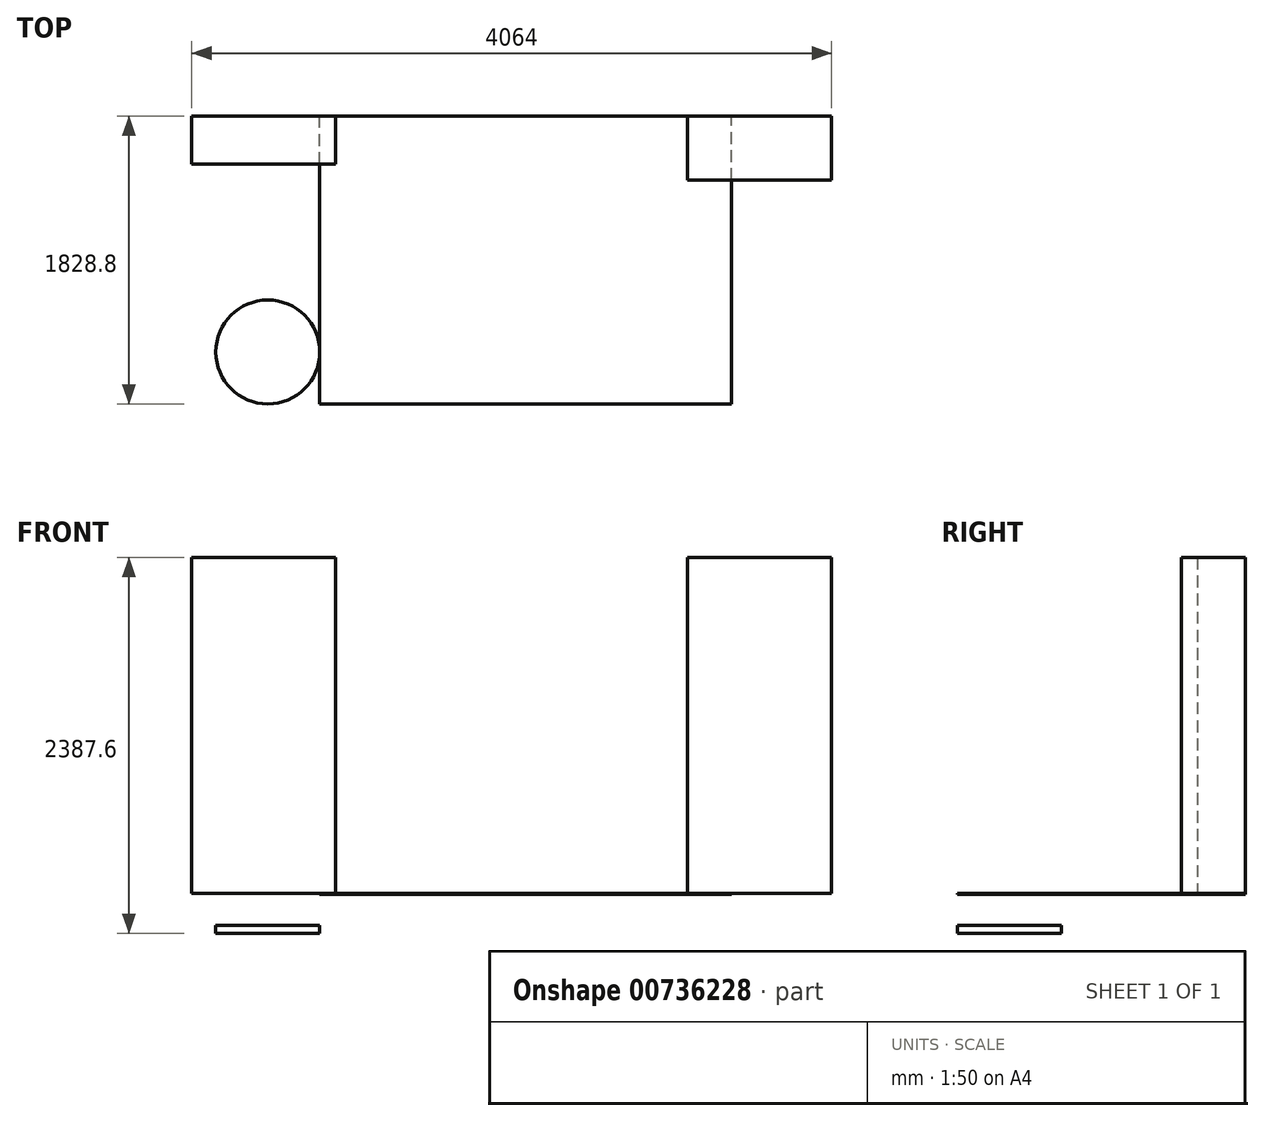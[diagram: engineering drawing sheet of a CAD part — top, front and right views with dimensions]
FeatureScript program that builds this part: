
annotation { "Feature Type Name" : "Feature", "Feature Type Description" : "" }
export const myFeature = defineFeature(function(context is Context, id is Id, definition is map)
    precondition{}
    {
        {
            assignVariable(context, id + "F0", {"name" : "StoopT", "anyValue" : 6});
        }
        {
            var Q0;
            Q0=qCreatedBy(makeId("Top.planeOp"),FACE);
            var sketch = newSketch(context, id + "F1", { "sketchPlane" : qUnion([Q0])});
            skLineSegment(sketch, "E0.bottom", {"start": v(1308.1, -914.4) * mm, "end": v(-1308.1, -914.4) * mm});
            skLineSegment(sketch, "E0.top", {"start": v(1308.1, 914.4) * mm, "end": v(-1308.1, 914.4) * mm});
            skLineSegment(sketch, "E0.left", {"start": v(1308.1, -914.4) * mm, "end": v(1308.1, 914.4) * mm});
            skLineSegment(sketch, "E0.right", {"start": v(-1308.1, -914.4) * mm, "end": v(-1308.1, 914.4) * mm});
            skPoint(sketch, "E0.middle", {"position": v(0, 0) * mm});
            skSolve(sketch);
        }
        {
            var Q0;
            Q0=makeQuery(id+"F1.imprint","IMPRINT",FACE,{"disambiguationData":[TD([[makeQuery(id+"F1.imprint","IMPRINT",EDGE,{"derivedFrom":sQuery(id+"F1.wireOp",EDGE,"E0.bottom")}),-1.0]])]});
            extrude(context, id + "F2", {"entities" : qUnion([Q0]), "depth" : (getVariable(context, 'StoopT')) * mm, "offsetDistance" : 25.4 * mm});
        }
        {
            var Q0;
            Q0=makeQuery(id+"F2.opExtrude","CAP_FACE",FACE,{"disambiguationData":[OSD([sQuery(id+"F1.wireOp",EDGE,"E0.bottom"),sQuery(id+"F1.wireOp",EDGE,"E0.top"),sQuery(id+"F1.wireOp",EDGE,"E0.left"),sQuery(id+"F1.wireOp",EDGE,"E0.right")])],"isStart":false});
            var sketch = newSketch(context, id + "F3", { "sketchPlane" : qUnion([Q0])});
            skLineSegment(sketch, "E1.top", {"start": v(-2120.9, 609.6) * mm, "end": v(-1206.5, 609.6) * mm});
            skLineSegment(sketch, "E1.left", {"start": v(-2120.9, 914.4) * mm, "end": v(-2120.9, 609.6) * mm});
            skLineSegment(sketch, "E1.right", {"start": v(-1206.5, 914.4) * mm, "end": v(-1206.5, 609.6) * mm});
            skLineSegment(sketch, "E2.bottom", {"start": v(1943.1, 914.4) * mm, "end": v(1028.7, 914.4) * mm});
            skLineSegment(sketch, "E2.top", {"start": v(1943.1, 508) * mm, "end": v(1028.7, 508) * mm});
            skLineSegment(sketch, "E2.left", {"start": v(1943.1, 914.4) * mm, "end": v(1943.1, 508) * mm});
            skLineSegment(sketch, "E2.right", {"start": v(1028.7, 914.4) * mm, "end": v(1028.7, 508) * mm});
            skLineSegment(sketch, "E3", {"start": v(-2120.9, 914.4) * mm, "end": v(-1206.5, 914.4) * mm});
            skSolve(sketch);
        }
        {
            var Q0;
            {var subQ0=sQuery(id+"F3.wireOp",EDGE,"E1.left");Q0=makeQuery(id+"F3.imprint","IMPRINT",FACE,{"disambiguationData":[TD([[makeQuery(id+"F3.imprint","IMPRINT",EDGE,{"derivedFrom":subQ0}),1.0]])]});}
            var Q1;
            {var subQ0=sQuery(id+"F3.wireOp",EDGE,"E1.right");Q1=makeQuery(id+"F3.imprint","IMPRINT",FACE,{"disambiguationData":[TD([[makeQuery(id+"F3.imprint","IMPRINT",EDGE,{"derivedFrom":subQ0}),-1.0]])]});}
            var Q2;
            {var subQ3=sQuery(id+"F3.wireOp",EDGE,"E2.right");Q2=makeQuery(id+"F3.imprint","IMPRINT",FACE,{"disambiguationData":[TD([[makeQuery(id+"F3.imprint","IMPRINT",EDGE,{"derivedFrom":subQ3}),1.0]])]});}
            var Q3;
            {var subQ3=sQuery(id+"F3.wireOp",EDGE,"E2.left");Q3=makeQuery(id+"F3.imprint","IMPRINT",FACE,{"disambiguationData":[TD([[makeQuery(id+"F3.imprint","IMPRINT",EDGE,{"derivedFrom":subQ3}),-1.0]])]});}
            extrude(context, id + "F4", {"entities" : qUnion([Q0, Q1, Q2, Q3]), "depth" : 2133.6 * mm, "offsetDistance" : 25.4 * mm});
        }
        {
            var Q0;
            Q0=makeQuery(id+"F2.opExtrude","CAP_FACE",FACE,{"disambiguationData":[OSD([sQuery(id+"F1.wireOp",EDGE,"E0.bottom"),sQuery(id+"F1.wireOp",EDGE,"E0.top"),sQuery(id+"F1.wireOp",EDGE,"E0.left"),sQuery(id+"F1.wireOp",EDGE,"E0.right")])],"isStart":false});
            cPlane(context, id + "F5", {"entities" : qUnion([Q0]), "cplaneType" : CPlaneType.OFFSET, "offset" : 203.2 * mm, "oppositeDirection" : true, "width" : 152.4 * mm, "height" : 152.4 * mm});
        }
        {
            var Q0;
            Q0=qCreatedBy(id+"F5.planeOp",FACE);
            var sketch = newSketch(context, id + "F6", { "sketchPlane" : qUnion([Q0])});
            skLineSegment(sketch, "E4.0", {"start": v(-1308.1, -914.4) * mm, "end": v(-1308.1, 914.4) * mm, "construction": true});
            skLineSegment(sketch, "E5", {"start": v(-1308.1, -584.2) * mm, "end": v(-1638.3, -584.2) * mm, "construction": true});
            skCircle(sketch, "E6", {"center": v(-1638.3, -584.2) * mm, "radius": 330.2 * mm});
            skSolve(sketch);
        }
        {
            var Q0;
            Q0=makeQuery(id+"F6.imprint","IMPRINT",FACE,{"disambiguationData":[TD([[makeQuery(id+"F6.imprint","IMPRINT",EDGE,{"derivedFrom":sQuery(id+"F6.wireOp",EDGE,"E6")}),1.0]])]});
            extrude(context, id + "F7", {"entities" : qUnion([Q0]), "oppositeDirection" : true, "depth" : 50.8 * mm, "offsetDistance" : 25.4 * mm});
        }
    });
